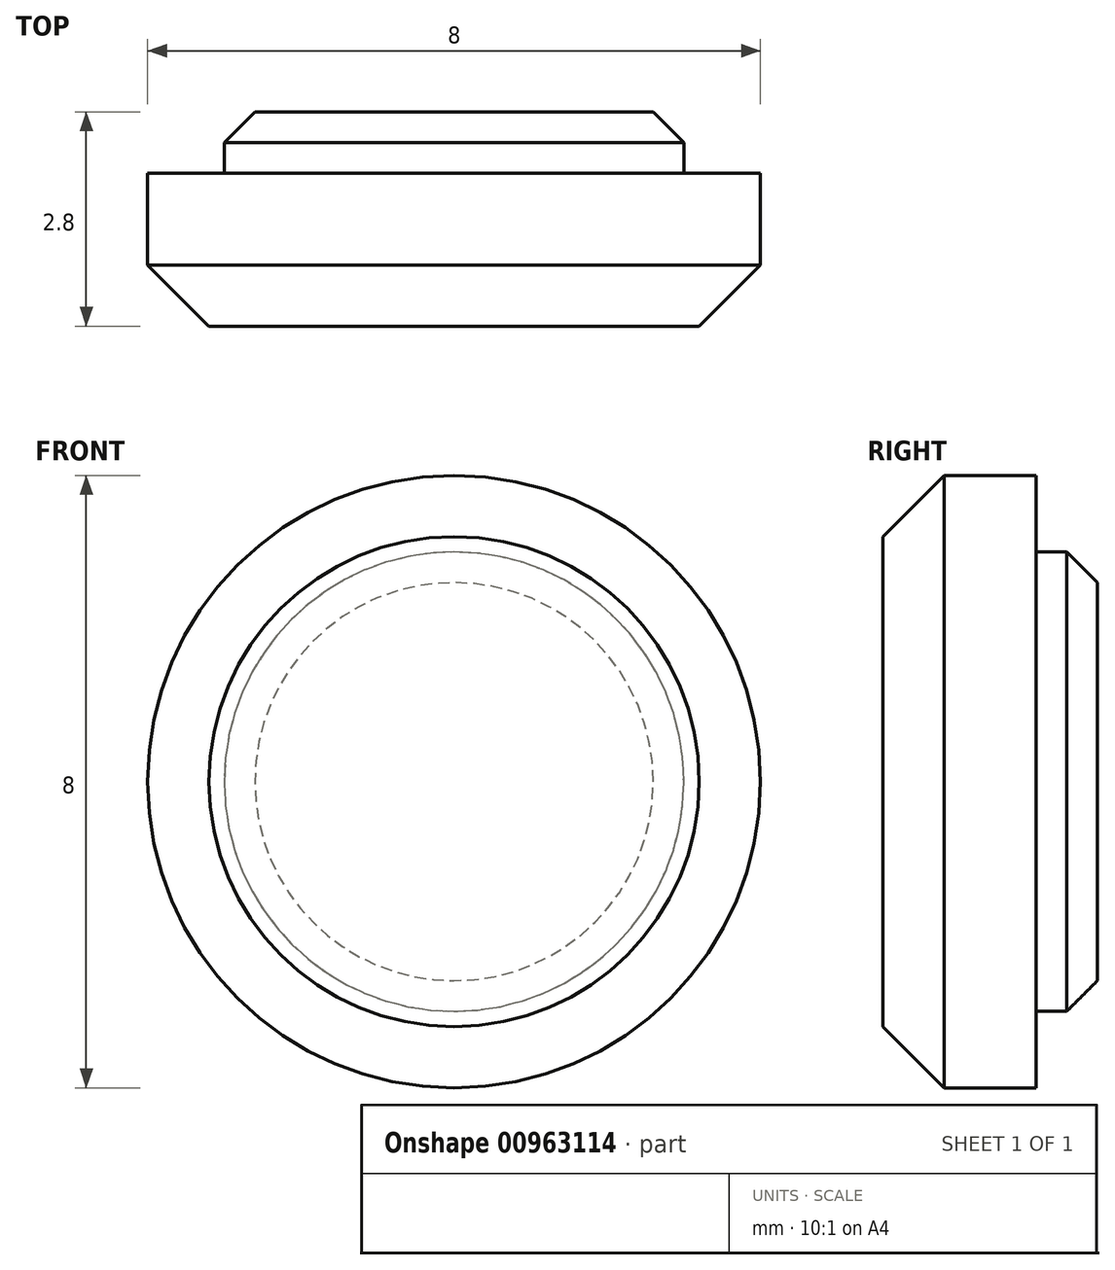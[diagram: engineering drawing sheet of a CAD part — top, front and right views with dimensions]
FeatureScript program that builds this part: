
annotation { "Feature Type Name" : "Feature", "Feature Type Description" : "" }
export const myFeature = defineFeature(function(context is Context, id is Id, definition is map)
    precondition{}
    {
        {
            var Q0;
            Q0=qCreatedBy(makeId("Right.planeOp"),FACE);
            var sketch = newSketch(context, id + "F0", { "sketchPlane" : qUnion([Q0])});
            skLineSegment(sketch, "E0", {"start": v(-2, 0) * mm, "end": v(-2, 4) * mm});
            skLineSegment(sketch, "E1", {"start": v(-2, 4) * mm, "end": v(0, 4) * mm});
            skLineSegment(sketch, "E2", {"start": v(0, 4) * mm, "end": v(0, 3) * mm});
            skLineSegment(sketch, "E3", {"start": v(0, 3) * mm, "end": v(0.8, 3) * mm});
            skLineSegment(sketch, "E4", {"start": v(0.8, 3) * mm, "end": v(0.8, 0) * mm});
            skLineSegment(sketch, "E5", {"start": v(0.8, 0) * mm, "end": v(-2, 0) * mm});
            skSolve(sketch);
        }
        {
            var Q0;
            Q0 = qSketchRegion(id + "F0", true);
            var Q1;
            Q1=sQuery(id+"F0.wireOp",EDGE,"E5");
            revolve(context, id + "F1", {"surfaceOperationType" : NewSurfaceOperationType.NEW, "entities" : qUnion([Q0]), "axis" : qUnion([Q1]), "revolveType" : RevolveType.FULL});
        }
        {
            var Q0;
            Q0=makeQuery(id+"F1.opRevolve","SWEPT_EDGE",EDGE,{"disambiguationData":[OSD([sQuery(id+"F0.wireOp",EDGE,"E0"),sQuery(id+"F0.wireOp",EDGE,"E1")])]});
            chamfer(context, id + "F2", {"entities" : qUnion([Q0]), "width" : 0.8 * mm, "tangentPropagation" : true});
        }
        {
            var Q0;
            Q0=makeQuery(id+"F1.opRevolve","SWEPT_EDGE",EDGE,{"disambiguationData":[OSD([sQuery(id+"F0.wireOp",EDGE,"E3"),sQuery(id+"F0.wireOp",EDGE,"E4")])]});
            chamfer(context, id + "F3", {"entities" : qUnion([Q0]), "width" : 0.4 * mm, "tangentPropagation" : true});
        }
    });
